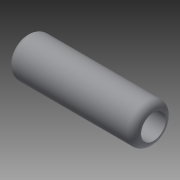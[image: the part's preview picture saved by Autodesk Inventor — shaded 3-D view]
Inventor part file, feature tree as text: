
AUTODESK INVENTOR PART (.ipt)
format: ipt  version: 2015 (Build 190159000, 159)  size: 109,056 bytes
history: native  units: in
note: dims shown in document units (in); Inventor stores cm internally (conversion verified against a paired STEP export)
features: fillet x2, revolve x1, sketch x1
ambient origin geometry x8: Origin, YZ Plane, XZ Plane, XY Plane, X Axis, Y Axis, Z Axis, Center Point
bodies: Solid1 (feature_tree)
feature tree (4):
  revolve  "Revolution1"  Angle=360.0deg
  fillet  "Fillet1"  Radius=0.25in
  fillet  "Fillet2"  Radius=0.25in
  sketch  "Sketch1"  dims[d3=4.469in d10=360.0deg d11=0.25in d12=0.25in]
